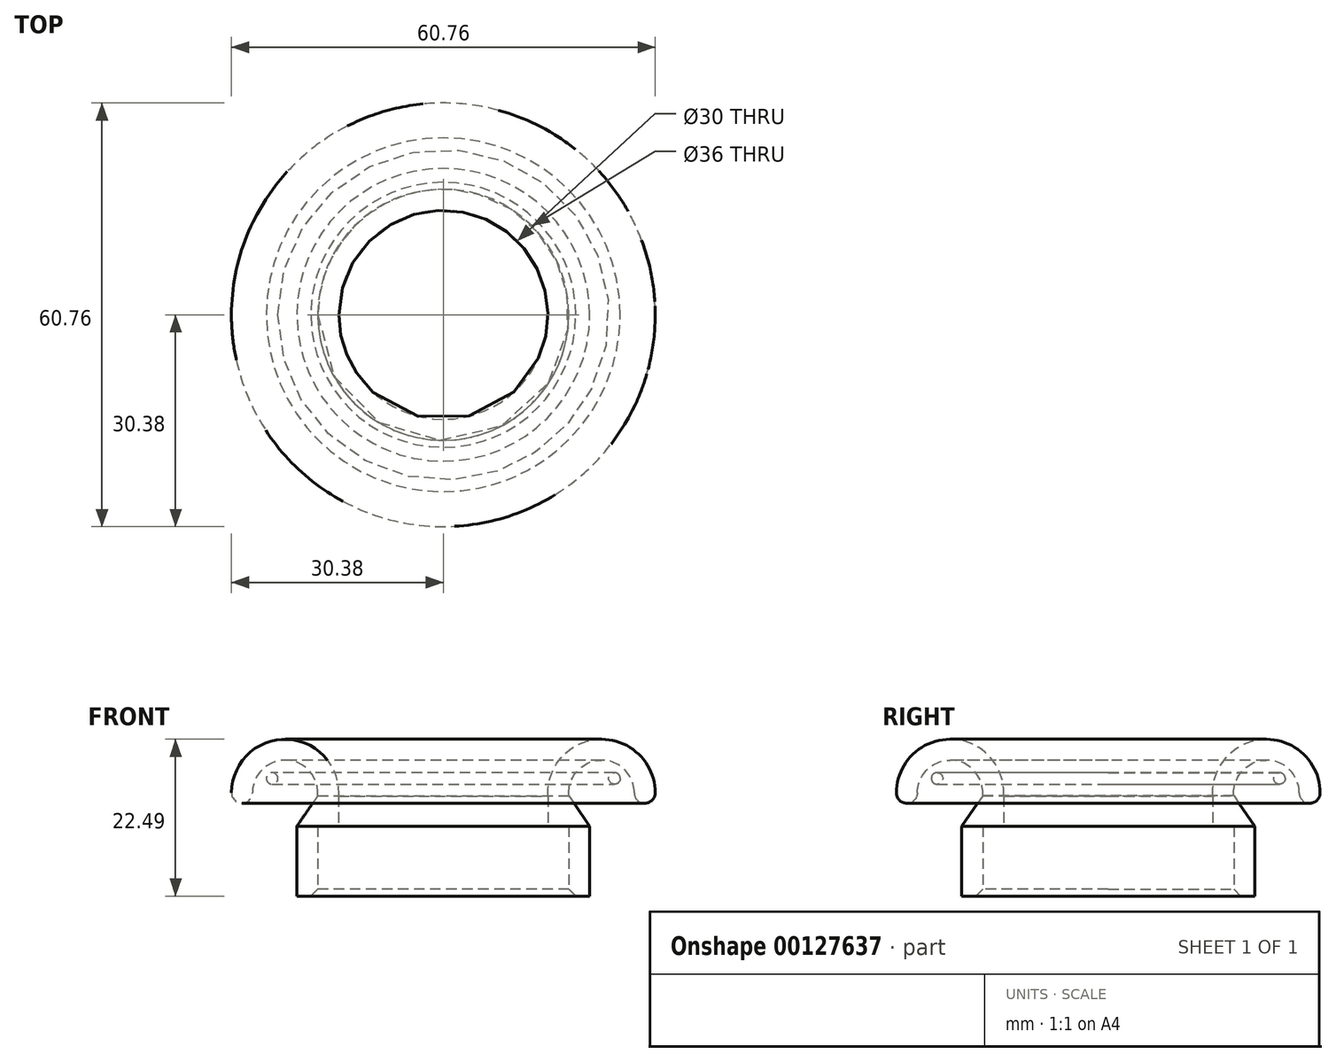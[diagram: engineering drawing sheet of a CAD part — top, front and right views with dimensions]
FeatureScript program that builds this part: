
annotation { "Feature Type Name" : "Feature", "Feature Type Description" : "" }
export const myFeature = defineFeature(function(context is Context, id is Id, definition is map)
    precondition{}
    {
        {
            var Q0;
            Q0=qCreatedBy(makeId("Front.planeOp"),FACE);
            var sketch = newSketch(context, id + "F0", { "sketchPlane" : qUnion([Q0])});
            skPoint(sketch, "E0.second.point", {"position": v(77.54, 18.1) * mm});
            skPoint(sketch, "E0.third.point", {"position": v(37.2, 56.24) * mm});
            skPoint(sketch, "E1.orphan", {"position": v(4.05, 0) * mm});
            skLineSegment(sketch, "E2", {"start": v(0, 0) * mm, "end": v(-15, 0) * mm});
            skLineSegment(sketch, "E3", {"start": v(-15, 0) * mm, "end": v(-15, 56.91) * mm});
            skCircle(sketch, "E4", {"center": v(9.55, 20) * mm, "radius": 0.83 * mm});
            skPoint(sketch, "E5.end.orphan", {"position": v(4.05, 10.65) * mm});
            skPoint(sketch, "E6.visualSharp", {"position": v(7.56, 0) * mm});
            skPoint(sketch, "E7.end.orphan", {"position": v(20.64, 18.1) * mm});
            skLineSegment(sketch, "E8", {"start": v(0, 18.1) * mm, "end": v(0, 17.69) * mm});
            skArc(sketch, "E9", {"start": v(15.38, 17.95) * mm, "mid": v(7.34, 25.61) * mm, "end": v(0.01, 17.27) * mm});
            skPoint(sketch, "E10.end.orphan", {"position": v(2.97, 14.17) * mm});
            skPoint(sketch, "E10.start.orphan", {"position": v(2.97, 14.04) * mm});
            skLineSegment(sketch, "E11", {"start": v(0, 18.1) * mm, "end": v(0, 13.1) * mm});
            skLineSegment(sketch, "E12", {"start": v(0, 17.69) * mm, "end": v(0.01, 17.27) * mm});
            skArc(sketch, "E13", {"start": v(2.63, 11.72) * mm, "mid": v(2.65, 11.7) * mm, "end": v(2.68, 11.68) * mm});
            skArc(sketch, "E14", {"start": v(1.67, 18.13) * mm, "mid": v(1.67, 18.03) * mm, "end": v(1.67, 17.93) * mm});
            skLineSegment(sketch, "E15", {"start": v(1.67, 18.13) * mm, "end": v(1.67, 13.13) * mm});
            skLineSegment(sketch, "E16", {"start": v(0, 13.1) * mm, "end": v(0, 0) * mm});
            skLineSegment(sketch, "E17", {"start": v(0, 13.1) * mm, "end": v(3, 13.13) * mm});
            skLineSegment(sketch, "E18", {"start": v(3, 13.13) * mm, "end": v(3, 3.13) * mm});
            skLineSegment(sketch, "E19.0", {"start": v(6, 13.13) * mm, "end": v(6, 3.13) * mm});
            skArc(sketch, "E20.0", {"start": v(12.38, 17.94) * mm, "mid": v(7.47, 22.62) * mm, "end": v(3, 17.52) * mm});
            skLineSegment(sketch, "E21", {"start": v(3, 17.52) * mm, "end": v(6, 13.13) * mm});
            skArc(sketch, "E22", {"start": v(15.38, 17.95) * mm, "mid": v(13.88, 16.45) * mm, "end": v(12.38, 17.94) * mm});
            skLineSegment(sketch, "E23", {"start": v(6, 3.13) * mm, "end": v(3, 3.13) * mm});
            skSolve(sketch);
        }
        {
            var Q0;
            Q0 = qSketchRegion(id + "F0", true);
            var Q1;
            Q1=sQuery(id+"F0.wireOp",EDGE,"E3");
            revolve(context, id + "F1", {"entities" : qUnion([Q0]), "axis" : qUnion([Q1]), "revolveType" : RevolveType.FULL});
        }
        {
            var Q0;
            Q0=makeQuery(id+"F1.opRevolve","SWEPT_EDGE",EDGE,{"disambiguationData":[OSD([sQuery(id+"F0.wireOp",EDGE,"E18"),sQuery(id+"F0.wireOp",EDGE,"E23")])]});
            chamfer(context, id + "F2", {"entities" : qUnion([Q0]), "width" : 1 * mm, "tangentPropagation" : true});
        }
    });
